# Revit family: QF_ELECTROLUXPROFESSIONAL_511063_TW12SLCB
name_source: partatom
category: Attrezzature speciali
units: mm (PartAtom-declared; Revit-internal decimal feet)

## family parameters
Basato su piano di lavoro = No
Condiviso = No
Punto di calcolo locali = No
Quota connettore circolare = Usa diametro
Sempre verticale = Sì
Taglio con vuoti quando caricato = No
Tipo di parte = Normale

## types (1)
- Standard
    Accessory = Sì
    Cold Water Size = 19 mm
    Compressed Air Pressure = 0.0 Pa
    Compressed Air Size = 0 mm
    Compressed Air Volume = 0.0 L/s
    Condensate Return Size = 19 mm
    Cycle = 50 Hz
    Depth Actual = 824 mm  [stored 2.70341 ft]
    Descrizione = TRAYWASHER,STEAM,C.U, DRYER, L>R,1200T/H
    Direct Waste Size = 50 mm
    Gas Input Pressure = 0
    Gas KW = 0
    Gas Size = 0 mm
    HP = 8.6 HP
    Height Actual = 1914 mm  [stored 6.27953 ft]
    Hot Water Size = 19 mm
    Item Number = 511063
    Length Actual = 2980 mm  [stored 9.7769 ft]
    Modello = TW12SLCB
    Phase = 3
    Produttore = Electrolux Professional
    Prospetto di default = 0 mm  [stored 0 ft]
    Refrigerant Compressor Remote = Sì
    Refrigeration Liquid Line Size = 0 mm  [stored 0 ft]
    Refrigeration Suction Line Size = 0 mm  [stored 0 ft]
    Steam Consumption per Hour = 34
    Steam Supply Maximum Pressure = 9.8 Pa
    Steam Supply Minimum Pressure = 1.6 Pa
    Steam Supply Size = 19 mm
    URL = https://www.electroluxprofessional.com
    URL Manufacturer = https://www.electroluxprofessional.com
    Volts = 400 V
    Watts = 6400 W
    Weight = 520.00 kg

note: source unit labels omitted for Gas Input Pressure — the stored unit's dimension contradicts the parameter name (converter mislabeling)

note: [stored X ft] marks values corroborated as IEEE doubles in the binary element streams (Revit-internal decimal feet)

## geometry (parser evidence)
native form markers: Blend x2, Sweep x3
no freeform markers — native parametric forms only
